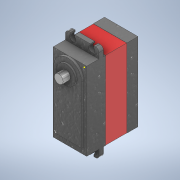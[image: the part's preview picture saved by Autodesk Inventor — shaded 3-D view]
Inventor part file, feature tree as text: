
AUTODESK INVENTOR PART (.ipt)
format: ipt  version: 2021 (Build 250183000, 183)  size: 226,304 bytes
history: native  units: mm
features: sketch x8, extrude x7, projected_geometry x2, plane x1, fillet x1
ambient origin geometry x8: Origin, YZ Plane, XZ Plane, XY Plane, X Axis, Y Axis, Z Axis, Center Point
bodies: Solid1 (feature_tree)
feature tree (19):
  extrude  "Extrusion1"  Depth=70.0mm
  extrude  "Extrusion2"  Depth=19.0mm TaperAngle=0.0deg
  extrude  "Extrusion3"  Depth=17.0mm
  extrude  "Extrusion4"  Depth=1.5mm
  extrude  "Extrusion5"  [1 undecoded]
  plane  "Work Plane1"
  extrude  "Extrusion6"  Depth=8.0mm
  fillet  "Fillet1"  Radius=5.5mm
  sketch  "Sketch7"  dims[d18=5.5mm d19=3.5mm d20=3.5mm d21=6.5mm]
  extrude  "Extrusion7"  Depth=3.5mm
  sketch  "Sketch1"  dims[d0=30.0mm d1=70.0mm]
  sketch  "Sketch2"  dims[d2=10.0mm d3=0.0mm d4=19.0mm d5=0.0mm]
  projected_geometry  "Projected Loop1"
  sketch  "Sketch3"  dims[d6=19.0mm d7=0.0mm d8=17.0mm]
  projected_geometry  "Projected Loop2"
  sketch  "Sketch4"  dims[d9=1.5mm d10=0.0mm d11=7.8mm]
  sketch  "Sketch5"  dims[d12=6.5mm d13=0.0mm d14=-17.0mm]
  sketch  "Sketch6"  dims[d15=30.0mm d16=8.0mm d17=5.5mm]
  sketch  "Sketch8"  dims[d22=6.5mm d23=4.0mm d24=0.0mm d25=3.0mm d26=12.5mm d27=2.0mm d28=0.0mm d29=0.1mm d30=0.1mm d31=0.1mm]
note: 1 required parameter value undecoded (feature->parameter linkage not recoverable at this tier; creation-order binding heuristic only, values carry confidence <= 0.55)
